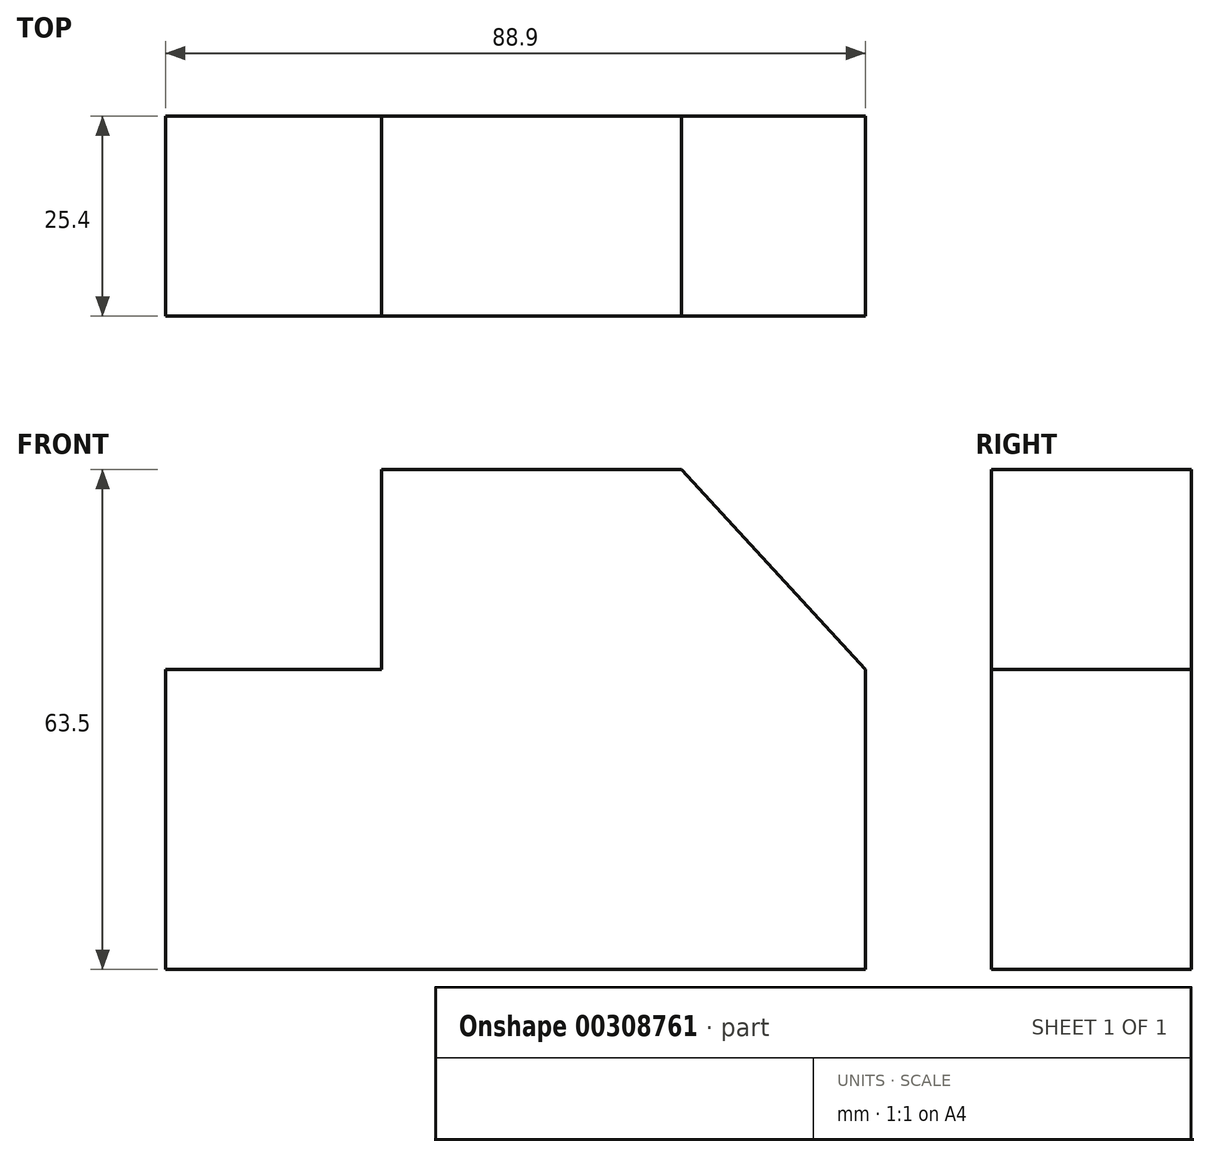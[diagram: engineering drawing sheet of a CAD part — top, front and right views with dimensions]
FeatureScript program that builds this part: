
annotation { "Feature Type Name" : "Feature", "Feature Type Description" : "" }
export const myFeature = defineFeature(function(context is Context, id is Id, definition is map)
    precondition{}
    {
        {
            var Q0;
            Q0=qCreatedBy(makeId("Front.planeOp"),FACE);
            var sketch = newSketch(context, id + "F0", { "sketchPlane" : qUnion([Q0])});
            skLineSegment(sketch, "E0", {"start": v(-41.35, -47.62) * mm, "end": v(47.55, -47.62) * mm});
            skLineSegment(sketch, "E1", {"start": v(47.55, -47.62) * mm, "end": v(47.55, -9.52) * mm});
            skLineSegment(sketch, "E2", {"start": v(47.55, -9.52) * mm, "end": v(24.18, 15.88) * mm});
            skLineSegment(sketch, "E3", {"start": v(24.18, 15.88) * mm, "end": v(-13.92, 15.88) * mm});
            skLineSegment(sketch, "E4", {"start": v(-13.92, 15.88) * mm, "end": v(-13.92, -9.52) * mm});
            skLineSegment(sketch, "E5", {"start": v(-13.92, -9.52) * mm, "end": v(-41.35, -9.52) * mm});
            skLineSegment(sketch, "E6", {"start": v(-41.35, -9.52) * mm, "end": v(-41.35, -47.62) * mm});
            skSolve(sketch);
        }
        {
            var Q0;
            Q0=makeQuery(id+"F0.imprint","IMPRINT",FACE,{"disambiguationData":[TD([[makeQuery(id+"F0.imprint","IMPRINT",EDGE,{"derivedFrom":sQuery(id+"F0.wireOp",EDGE,"E0")}),1.0]])]});
            extrude(context, id + "F1", {"entities" : qUnion([Q0]), "depth" : 25.4 * mm});
        }
    });
